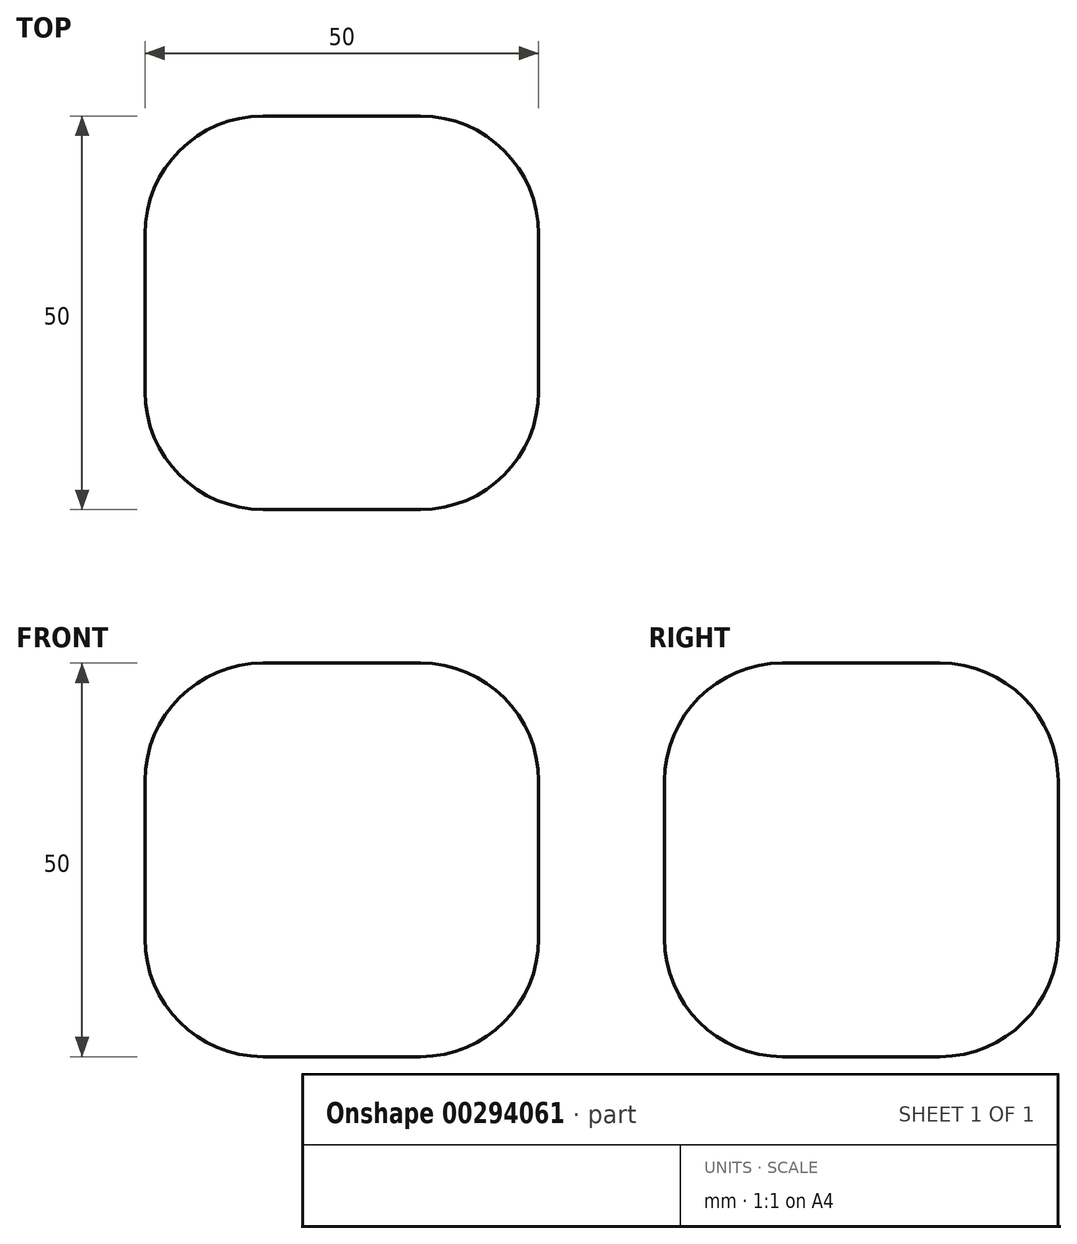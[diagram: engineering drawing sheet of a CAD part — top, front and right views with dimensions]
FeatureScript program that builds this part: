
annotation { "Feature Type Name" : "Feature", "Feature Type Description" : "" }
export const myFeature = defineFeature(function(context is Context, id is Id, definition is map)
    precondition{}
    {
        {
            var Q0;
            Q0=qCreatedBy(makeId("Top.planeOp"),FACE);
            var sketch = newSketch(context, id + "F0", { "sketchPlane" : qUnion([Q0])});
            skLineSegment(sketch, "E0.bottom", {"start": v(-25, 25) * mm, "end": v(25, 25) * mm});
            skLineSegment(sketch, "E0.top", {"start": v(-25, -25) * mm, "end": v(25, -25) * mm});
            skLineSegment(sketch, "E0.left", {"start": v(-25, 25) * mm, "end": v(-25, -25) * mm});
            skLineSegment(sketch, "E0.right", {"start": v(25, 25) * mm, "end": v(25, -25) * mm});
            skPoint(sketch, "E0.middle", {"position": v(0, 0) * mm});
            skSolve(sketch);
        }
        {
            var Q0;
            Q0=makeQuery(id+"F0.imprint","IMPRINT",FACE,{"disambiguationData":[TD([[makeQuery(id+"F0.imprint","IMPRINT",EDGE,{"derivedFrom":sQuery(id+"F0.wireOp",EDGE,"E0.bottom")}),-1.0]])]});
            extrude(context, id + "F1", {"entities" : qUnion([Q0]), "endBound" : BoundingType.SYMMETRIC, "depth" : 50 * mm});
        }
        {
            var Q0;
            Q0=makeQuery(id+"F1.opExtrude","CAP_EDGE",EDGE,{"disambiguationData":[OSD([sQuery(id+"F0.wireOp",EDGE,"E0.bottom")])],"isStart":false});
            var Q1;
            Q1=makeQuery(id+"F1.opExtrude","CAP_EDGE",EDGE,{"disambiguationData":[OSD([sQuery(id+"F0.wireOp",EDGE,"E0.bottom")])],"isStart":true});
            var Q2;
            Q2=makeQuery(id+"F1.opExtrude","SWEPT_EDGE",EDGE,{"disambiguationData":[OSD([sQuery(id+"F0.wireOp",EDGE,"E0.bottom"),sQuery(id+"F0.wireOp",EDGE,"E0.right")])]});
            var Q3;
            Q3=makeQuery(id+"F1.opExtrude","SWEPT_EDGE",EDGE,{"disambiguationData":[OSD([sQuery(id+"F0.wireOp",EDGE,"E0.bottom"),sQuery(id+"F0.wireOp",EDGE,"E0.left")])]});
            var Q4;
            Q4=makeQuery(id+"F1.opExtrude","CAP_EDGE",EDGE,{"disambiguationData":[OSD([sQuery(id+"F0.wireOp",EDGE,"E0.left")])],"isStart":false});
            var Q5;
            Q5=makeQuery(id+"F1.opExtrude","CAP_EDGE",EDGE,{"disambiguationData":[OSD([sQuery(id+"F0.wireOp",EDGE,"E0.top")])],"isStart":false});
            var Q6;
            Q6=makeQuery(id+"F1.opExtrude","CAP_EDGE",EDGE,{"disambiguationData":[OSD([sQuery(id+"F0.wireOp",EDGE,"E0.right")])],"isStart":false});
            var Q7;
            Q7=makeQuery(id+"F1.opExtrude","SWEPT_EDGE",EDGE,{"disambiguationData":[OSD([sQuery(id+"F0.wireOp",EDGE,"E0.top"),sQuery(id+"F0.wireOp",EDGE,"E0.left")])]});
            var Q8;
            Q8=makeQuery(id+"F1.opExtrude","CAP_EDGE",EDGE,{"disambiguationData":[OSD([sQuery(id+"F0.wireOp",EDGE,"E0.top")])],"isStart":true});
            var Q9;
            Q9=makeQuery(id+"F1.opExtrude","SWEPT_EDGE",EDGE,{"disambiguationData":[OSD([sQuery(id+"F0.wireOp",EDGE,"E0.top"),sQuery(id+"F0.wireOp",EDGE,"E0.right")])]});
            var Q10;
            Q10=makeQuery(id+"F1.opExtrude","CAP_EDGE",EDGE,{"disambiguationData":[OSD([sQuery(id+"F0.wireOp",EDGE,"E0.left")])],"isStart":true});
            var Q11;
            Q11=makeQuery(id+"F1.opExtrude","CAP_EDGE",EDGE,{"disambiguationData":[OSD([sQuery(id+"F0.wireOp",EDGE,"E0.right")])],"isStart":true});
            fillet(context, id + "F2", {"entities" : qUnion([Q0, Q1, Q2, Q3, Q4, Q5, Q6, Q7, Q8, Q9, Q10, Q11]), "radius" : 15 * mm, "tangentPropagation" : true, "allowEdgeOverflow" : false});
        }
    });
